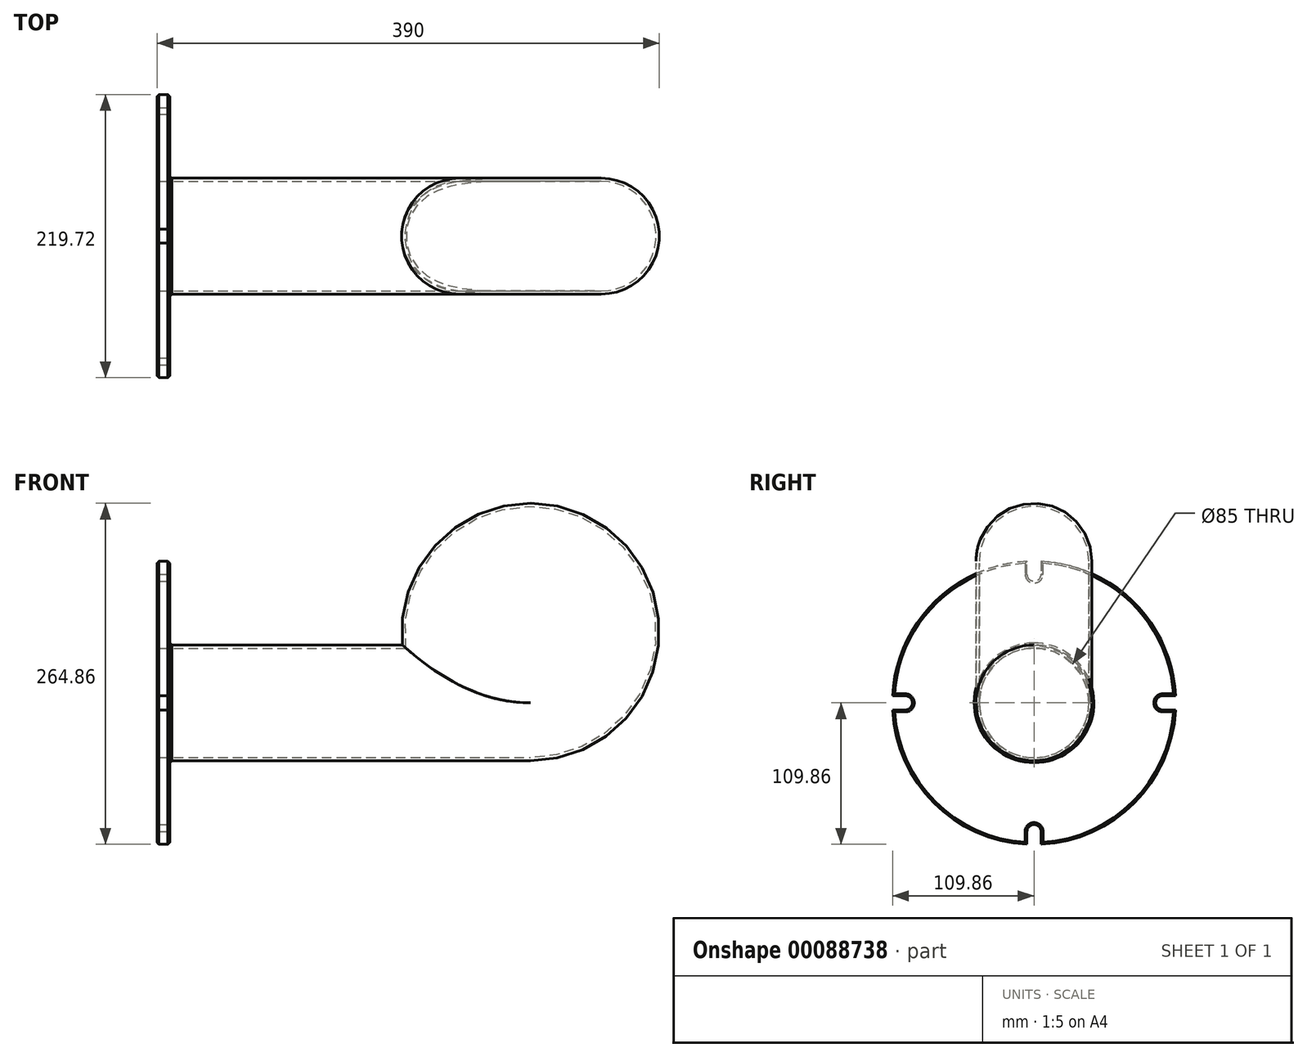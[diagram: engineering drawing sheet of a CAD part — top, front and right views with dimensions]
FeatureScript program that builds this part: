
annotation { "Feature Type Name" : "Feature", "Feature Type Description" : "" }
export const myFeature = defineFeature(function(context is Context, id is Id, definition is map)
    precondition{}
    {
        {
            var Q0;
            Q0=qCreatedBy(makeId("Front.planeOp"),FACE);
            var sketch = newSketch(context, id + "F0", { "sketchPlane" : qUnion([Q0])});
            skCircle(sketch, "E0", {"center": v(0, 0) * mm, "radius": 100 * mm});
            skLineSegment(sketch, "E1.bottom", {"start": v(0, -100) * mm, "end": v(-280, -100) * mm});
            skLineSegment(sketch, "E1.top", {"start": v(0, -10) * mm, "end": v(-280, -10) * mm});
            skLineSegment(sketch, "E1.left", {"start": v(0, -100) * mm, "end": v(0, -10) * mm});
            skLineSegment(sketch, "E1.right", {"start": v(-280, -100) * mm, "end": v(-280, -10) * mm});
            skSolve(sketch);
        }
        {
            var Q0;
            Q0=qSketchRegion(id+"F0",true);
            var Q1;
            {var subQ0=sQuery(id+"F0.wireOp",EDGE,"E1.bottom");Q1=makeQuery(id+"F0.imprint","IMPRINT",FACE,{"disambiguationData":[TD([[makeQuery(id+"F0.imprint","IMPRINT",EDGE,{"derivedFrom":subQ0}),-1.0]])]});}
            extrude(context, id + "F1", {"entities" : qUnion([Q0, Q1]), "depth" : 90 * mm, "symmetric" : true});
        }
        {
            var Q0;
            Q0=makeQuery(id+"F1.opExtrude","CAP_EDGE",EDGE,{"disambiguationData":[OSD([sQuery(id+"F0.wireOp",EDGE,"E1.top")])],"isStart":false});
            var Q1;
            Q1=makeQuery(id+"F1.opExtrude","CAP_EDGE",EDGE,{"disambiguationData":[OSD([sQuery(id+"F0.wireOp",EDGE,"E1.top")])],"isStart":true});
            var Q2;
            Q2=makeQuery(id+"F1.opExtrude","CAP_EDGE",EDGE,{"disambiguationData":[OSD([sQuery(id+"F0.wireOp",EDGE,"E1.bottom")])],"isStart":true});
            var Q3;
            Q3=makeQuery(id+"F1.opExtrude","CAP_EDGE",EDGE,{"disambiguationData":[OSD([sQuery(id+"F0.wireOp",EDGE,"E1.bottom")])],"isStart":false});
            fillet(context, id + "F2", {"entities" : qUnion([Q0, Q1, Q2, Q3]), "radius" : 45 * mm, "tangentPropagation" : true, "allowEdgeOverflow" : false});
        }
        {
            var Q0;
            Q0=makeQuery(id+"F1.opExtrude","SWEPT_FACE",FACE,{"disambiguationData":[OSD([sQuery(id+"F0.wireOp",EDGE,"E1.right")])]});
            var sketch = newSketch(context, id + "F3", { "sketchPlane" : qUnion([Q0])});
            skArc(sketch, "E2", {"start": v(-5.5, 54.86) * mm, "mid": v(-77.78, 22.78) * mm, "end": v(-109.86, -49.5) * mm});
            skArc(sketch, "E3", {"start": v(-5.5, 45.15) * mm, "mid": v(0, 39.5) * mm, "end": v(5.5, 45.15) * mm});
            skArc(sketch, "E4", {"start": v(-100.15, -60.5) * mm, "mid": v(-94.5, -55) * mm, "end": v(-100.15, -49.5) * mm});
            skArc(sketch, "E5", {"start": v(100.15, -49.5) * mm, "mid": v(94.5, -55) * mm, "end": v(100.15, -60.5) * mm});
            skArc(sketch, "E6", {"start": v(5.5, -155.15) * mm, "mid": v(0, -149.5) * mm, "end": v(-5.5, -155.15) * mm});
            skLineSegment(sketch, "E7", {"start": v(99.85, -49.5) * mm, "end": v(109.86, -49.5) * mm});
            skLineSegment(sketch, "E8", {"start": v(99.85, -60.5) * mm, "end": v(109.86, -60.5) * mm});
            skLineSegment(sketch, "E9", {"start": v(-5.5, -154.85) * mm, "end": v(-5.5, -164.86) * mm});
            skLineSegment(sketch, "E10", {"start": v(5.5, -154.85) * mm, "end": v(5.5, -164.86) * mm});
            skLineSegment(sketch, "E11", {"start": v(-99.85, -60.5) * mm, "end": v(-109.86, -60.5) * mm});
            skLineSegment(sketch, "E12", {"start": v(-99.85, -49.5) * mm, "end": v(-109.86, -49.5) * mm});
            skLineSegment(sketch, "E13", {"start": v(5.5, 44.85) * mm, "end": v(5.5, 54.86) * mm});
            skLineSegment(sketch, "E14", {"start": v(-5.5, 44.85) * mm, "end": v(-5.5, 54.86) * mm});
            skArc(sketch, "E15.trimOffspring", {"start": v(109.86, -49.5) * mm, "mid": v(77.78, 22.78) * mm, "end": v(5.5, 54.86) * mm});
            skArc(sketch, "E16.trimOffspring", {"start": v(5.5, -164.86) * mm, "mid": v(77.78, -132.78) * mm, "end": v(109.86, -60.5) * mm});
            skArc(sketch, "E17.trimOffspring", {"start": v(-109.86, -60.5) * mm, "mid": v(-77.78, -132.78) * mm, "end": v(-5.5, -164.86) * mm});
            skCircle(sketch, "E18", {"center": v(0, -55) * mm, "radius": 42.5 * mm});
            skSolve(sketch);
        }
        {
            var Q0;
            Q0=makeQuery(id+"F1.opExtrude","SWEPT_FACE",FACE,{"disambiguationData":[OSD([sQuery(id+"F0.wireOp",EDGE,"E1.right")])]});
            shell(context, id + "F4", {"entities" : qUnion([Q0]), "thickness" : 2.5 * mm});
        }
        {
            var Q0;
            Q0=qSketchRegion(id+"F3",true);
            var Q1;
            {var subQ1=sQuery(id+"F3.wireOp",EDGE,"E2");Q1=makeQuery(id+"F3.imprint","IMPRINT",FACE,{"disambiguationData":[TD([[makeQuery(id+"F3.imprint","IMPRINT",EDGE,{"derivedFrom":subQ1}),1.0]])]});}
            extrude(context, id + "F5", {"entities" : qUnion([Q0, Q1]), "operationType" : NewBodyOperationType.ADD, "depth" : 10 * mm});
        }
        {
            var Q0;
            Q0=makeQuery(id+"F5.opExtrude","CAP_FACE",FACE,{"disambiguationData":[OSD([sQuery(id+"F3.wireOp",EDGE,"E2"),sQuery(id+"F3.wireOp",EDGE,"E3"),sQuery(id+"F3.wireOp",EDGE,"E4"),sQuery(id+"F3.wireOp",EDGE,"E5"),sQuery(id+"F3.wireOp",EDGE,"E6"),sQuery(id+"F3.wireOp",EDGE,"E7"),sQuery(id+"F3.wireOp",EDGE,"E8"),sQuery(id+"F3.wireOp",EDGE,"E9"),sQuery(id+"F3.wireOp",EDGE,"E10"),sQuery(id+"F3.wireOp",EDGE,"E11"),sQuery(id+"F3.wireOp",EDGE,"E12"),sQuery(id+"F3.wireOp",EDGE,"E13"),sQuery(id+"F3.wireOp",EDGE,"E14"),sQuery(id+"F3.wireOp",EDGE,"E15.trimOffspring"),sQuery(id+"F3.wireOp",EDGE,"E16.trimOffspring"),sQuery(id+"F3.wireOp",EDGE,"E17.trimOffspring"),sQuery(id+"F3.wireOp",EDGE,"E18")])],"isStart":false});
            var Q1;
            Q1=makeQuery(id+"F5.opExtrude","CAP_FACE",FACE,{"disambiguationData":[OSD([sQuery(id+"F3.wireOp",EDGE,"E2"),sQuery(id+"F3.wireOp",EDGE,"E3"),sQuery(id+"F3.wireOp",EDGE,"E4"),sQuery(id+"F3.wireOp",EDGE,"E5"),sQuery(id+"F3.wireOp",EDGE,"E6"),sQuery(id+"F3.wireOp",EDGE,"E7"),sQuery(id+"F3.wireOp",EDGE,"E8"),sQuery(id+"F3.wireOp",EDGE,"E9"),sQuery(id+"F3.wireOp",EDGE,"E10"),sQuery(id+"F3.wireOp",EDGE,"E11"),sQuery(id+"F3.wireOp",EDGE,"E12"),sQuery(id+"F3.wireOp",EDGE,"E13"),sQuery(id+"F3.wireOp",EDGE,"E14"),sQuery(id+"F3.wireOp",EDGE,"E15.trimOffspring"),sQuery(id+"F3.wireOp",EDGE,"E16.trimOffspring"),sQuery(id+"F3.wireOp",EDGE,"E17.trimOffspring"),sQuery(id+"F3.wireOp",EDGE,"E18")])],"isStart":true});
            chamfer(context, id + "F6", {"entities" : qUnion([Q0, Q1]), "width" : 1.5 * mm, "tangentPropagation" : true});
        }
    });
